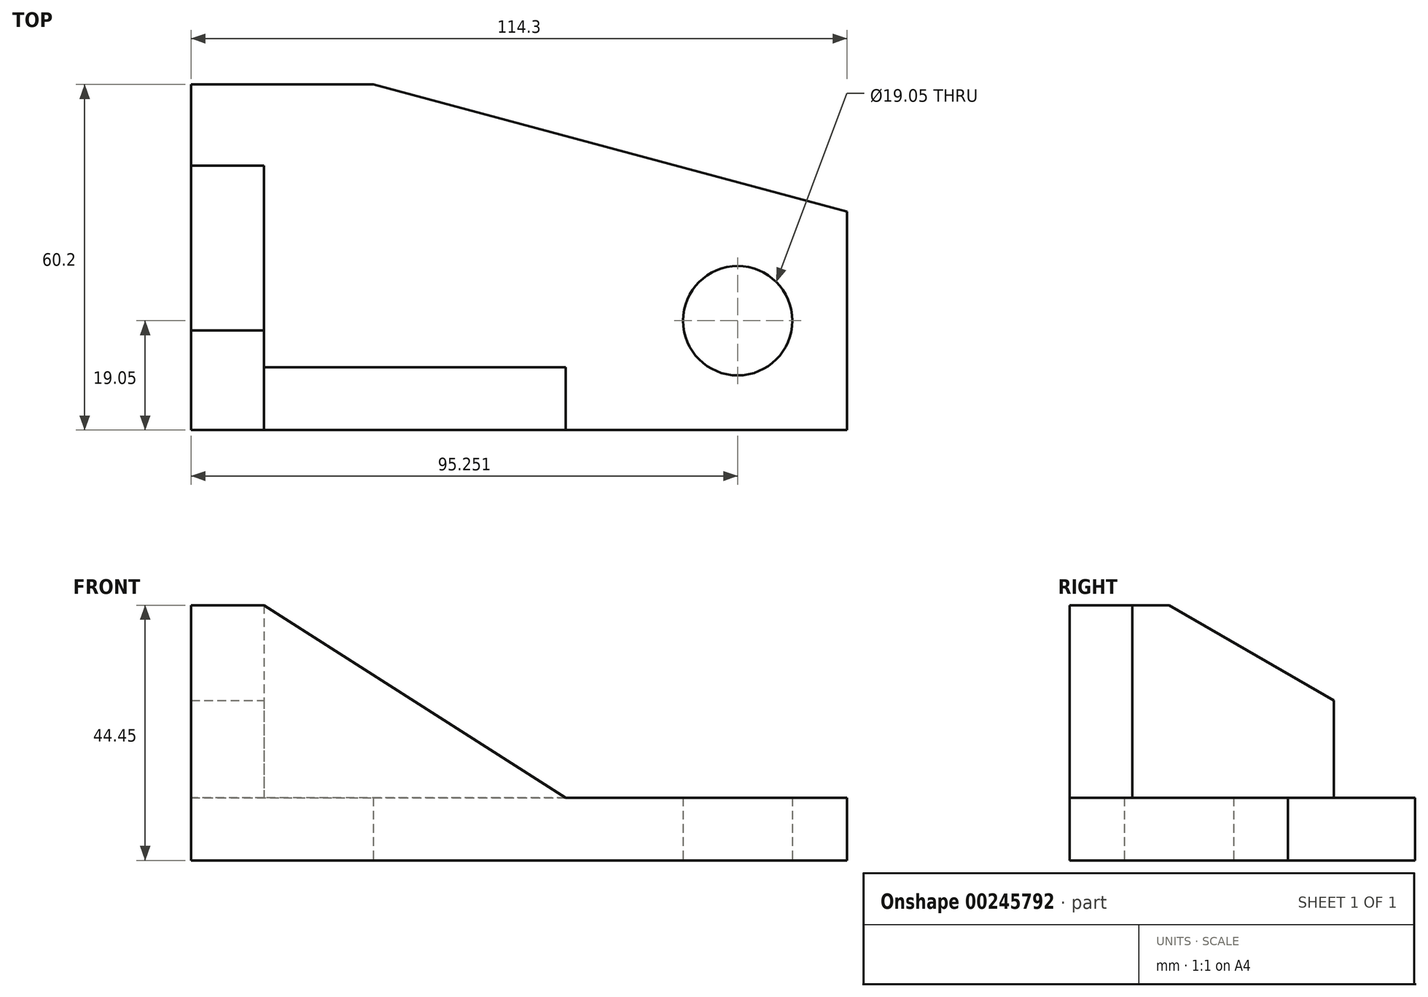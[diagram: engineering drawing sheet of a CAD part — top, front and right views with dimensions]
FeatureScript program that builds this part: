
annotation { "Feature Type Name" : "Feature", "Feature Type Description" : "" }
export const myFeature = defineFeature(function(context is Context, id is Id, definition is map)
    precondition{}
    {
        {
            var Q0;
            Q0=qCreatedBy(makeId("Top.planeOp"),FACE);
            var sketch = newSketch(context, id + "F0", { "sketchPlane" : qUnion([Q0])});
            skLineSegment(sketch, "E0.bottom", {"start": v(-61.28, 23.5) * mm, "end": v(-29.53, 23.5) * mm});
            skLineSegment(sketch, "E0.left", {"start": v(-61.28, 23.5) * mm, "end": v(-61.28, -36.7) * mm});
            skLineSegment(sketch, "E1", {"start": v(53.02, -36.7) * mm, "end": v(53.02, 1.38) * mm});
            skLineSegment(sketch, "E2.top", {"start": v(-61.28, 9.33) * mm, "end": v(-48.6, 9.33) * mm});
            skLineSegment(sketch, "E2.right", {"start": v(-48.6, -36.7) * mm, "end": v(-48.6, 9.33) * mm});
            skLineSegment(sketch, "E3", {"start": v(-29.53, 23.5) * mm, "end": v(53.02, 1.38) * mm});
            skLineSegment(sketch, "E4", {"start": v(-61.28, -36.7) * mm, "end": v(53.02, -36.7) * mm});
            skLineSegment(sketch, "E5", {"start": v(33.97, -36.7) * mm, "end": v(33.97, -1) * mm, "construction": true});
            skLineSegment(sketch, "E6", {"start": v(53.02, -17.65) * mm, "end": v(9.63, -17.65) * mm, "construction": true});
            skCircle(sketch, "E7", {"center": v(33.97, -17.65) * mm, "radius": 9.53 * mm});
            skLineSegment(sketch, "E8", {"start": v(-48.6, -25.78) * mm, "end": v(3.98, -25.78) * mm});
            skLineSegment(sketch, "E9", {"start": v(3.98, -25.78) * mm, "end": v(3.98, -36.7) * mm});
            skSolve(sketch);
        }
        {
            var Q0;
            Q0=makeQuery(id+"F0.imprint","IMPRINT",FACE,{"disambiguationData":[TD([[makeQuery(id+"F0.imprint","IMPRINT",EDGE,{"derivedFrom":sQuery(id+"F0.wireOp",EDGE,"E0.bottom")}),-1.0]])]});
            var Q1;
            {var subQ3=sQuery(id+"F0.wireOp",EDGE,"E8");Q1=makeQuery(id+"F0.imprint","IMPRINT",FACE,{"disambiguationData":[TD([[makeQuery(id+"F0.imprint","IMPRINT",EDGE,{"derivedFrom":subQ3}),-1.0]])]});}
            var Q2;
            {var subQ1=sQuery(id+"F0.wireOp",EDGE,"E2.top");Q2=makeQuery(id+"F0.imprint","IMPRINT",FACE,{"disambiguationData":[TD([[makeQuery(id+"F0.imprint","IMPRINT",EDGE,{"derivedFrom":subQ1}),-1.0]])]});}
            extrude(context, id + "F1", {"entities" : qUnion([Q0, Q1, Q2]), "depth" : 10.92 * mm});
        }
        {
            var Q0;
            {var subQ1=sQuery(id+"F0.wireOp",EDGE,"E2.top");Q0=makeQuery(id+"F0.imprint","IMPRINT",FACE,{"disambiguationData":[TD([[makeQuery(id+"F0.imprint","IMPRINT",EDGE,{"derivedFrom":subQ1}),-1.0]])]});}
            var Q1;
            {var subQ3=sQuery(id+"F0.wireOp",EDGE,"E8");Q1=makeQuery(id+"F0.imprint","IMPRINT",FACE,{"disambiguationData":[TD([[makeQuery(id+"F0.imprint","IMPRINT",EDGE,{"derivedFrom":subQ3}),-1.0]])]});}
            extrude(context, id + "F2", {"entities" : qUnion([Q0, Q1]), "operationType" : NewBodyOperationType.ADD, "depth" : 44.45 * mm});
        }
        {
            var Q0;
            Q0=makeQuery(id+"F2.opExtrude","SWEPT_FACE",FACE,{"disambiguationData":[OSD([sQuery(id+"F0.wireOp",EDGE,"E8")])]});
            var sketch = newSketch(context, id + "F3", { "sketchPlane" : qUnion([Q0])});
            skLineSegment(sketch, "E10", {"start": v(48.6, 44.45) * mm, "end": v(-3.98, 10.92) * mm});
            skSolve(sketch);
        }
        {
            var Q0;
            Q0=makeQuery(id+"F3.imprint","IMPRINT",FACE,{"disambiguationData":[TD([[makeQuery(id+"F3.imprint","IMPRINT",EDGE,{"derivedFrom":sQuery(id+"F3.wireOp",EDGE,"E10")}),-1.0]])]});
            extrude(context, id + "F4", {"entities" : qUnion([Q0]), "operationType" : NewBodyOperationType.REMOVE, "endBound" : BoundingType.THROUGH_ALL, "oppositeDirection" : true, "depth" : 25.4 * mm});
        }
        {
            var Q0;
            Q0=makeQuery(id+"F2.opExtrude","CAP_EDGE",EDGE,{"disambiguationData":[OSD([sQuery(id+"F0.wireOp",EDGE,"E2.top")])],"isStart":false});
            chamfer(context, id + "F5", {"entities" : qUnion([Q0]), "chamferType" : ChamferType.OFFSET_ANGLE, "width" : 28.7 * mm, "oppositeDirection" : true, "angle" : 30 * degree, "tangentPropagation" : true});
        }
    });
